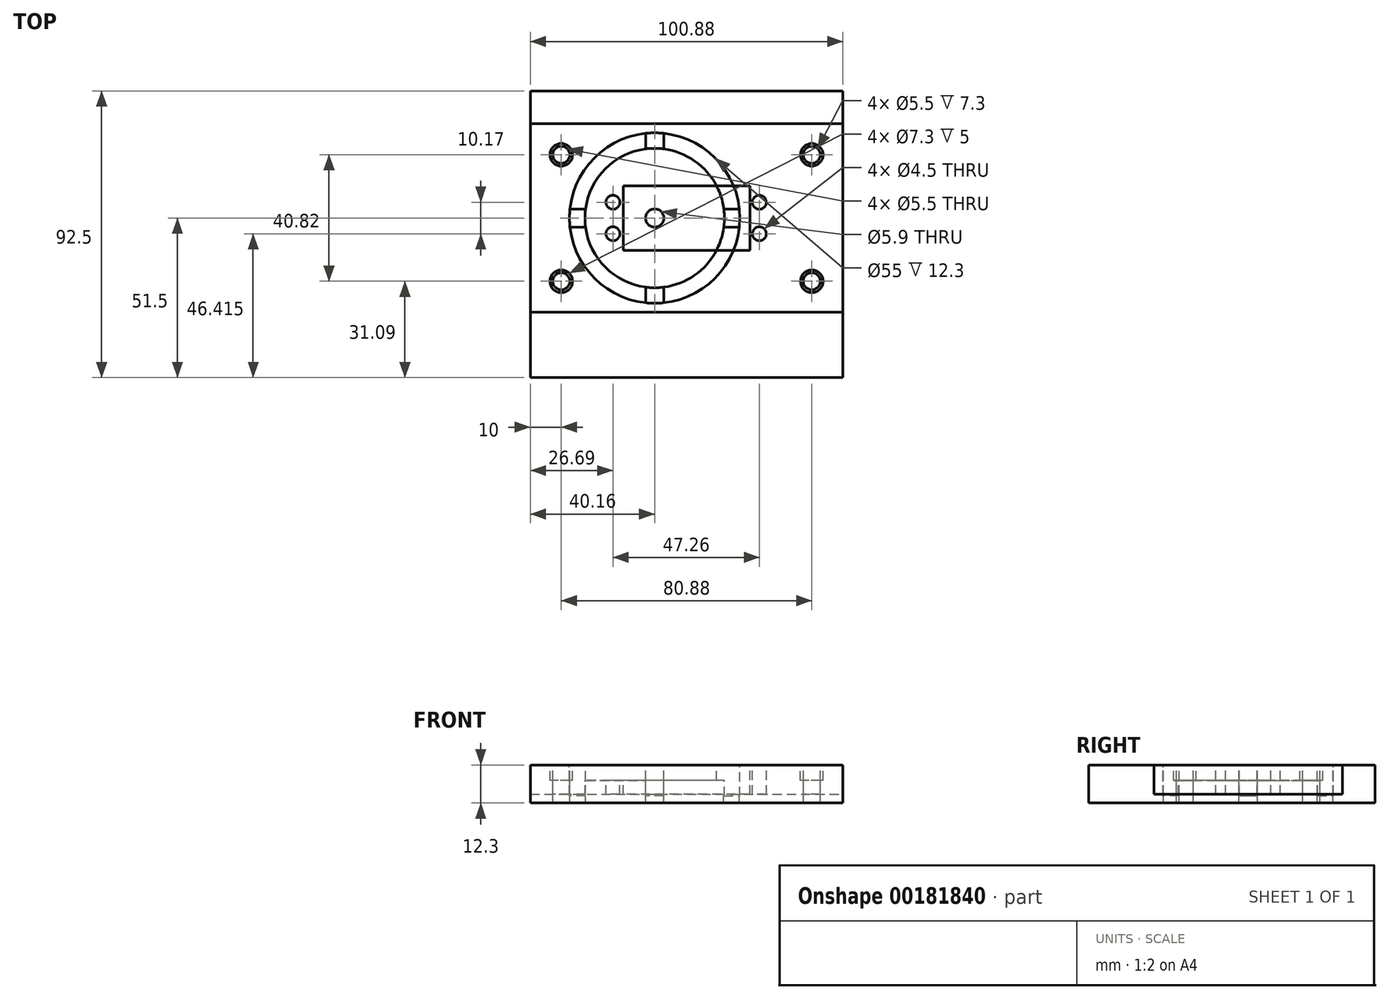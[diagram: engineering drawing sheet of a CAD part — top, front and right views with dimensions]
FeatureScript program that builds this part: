
annotation { "Feature Type Name" : "Feature", "Feature Type Description" : "" }
export const myFeature = defineFeature(function(context is Context, id is Id, definition is map)
    precondition{}
    {
        {
            var Q0;
            Q0=qCreatedBy(makeId("Top.planeOp"),FACE);
            var sketch = newSketch(context, id + "F0", { "sketchPlane" : qUnion([Q0])});
            skPoint(sketch, "E0.middle", {"position": v(0, 0) * mm});
            skLineSegment(sketch, "E1.bottom", {"start": v(19.94, 9.9) * mm, "end": v(-19.94, 9.9) * mm});
            skLineSegment(sketch, "E1.top", {"start": v(19.94, -9.91) * mm, "end": v(-19.94, -9.91) * mm});
            skLineSegment(sketch, "E1.left", {"start": v(19.94, 9.9) * mm, "end": v(19.94, -9.9) * mm});
            skLineSegment(sketch, "E1.right", {"start": v(-19.94, 9.9) * mm, "end": v(-19.94, -9.9) * mm});
            skPoint(sketch, "E2", {"position": v(-23.75, 5.08) * mm});
            skPoint(sketch, "E3", {"position": v(-23.75, -5.09) * mm});
            skPoint(sketch, "E4", {"position": v(23.5, 5.08) * mm});
            skPoint(sketch, "E5", {"position": v(23.5, -5.09) * mm});
            skPoint(sketch, "E6", {"position": v(-10.28, 0) * mm});
            skCircle(sketch, "E7", {"center": v(-23.75, 5.08) * mm, "radius": 2.19 * mm});
            skCircle(sketch, "E8", {"center": v(-23.75, -5.09) * mm, "radius": 2.19 * mm});
            skCircle(sketch, "E9", {"center": v(23.5, 5.08) * mm, "radius": 2.19 * mm});
            skCircle(sketch, "E10", {"center": v(23.5, -5.09) * mm, "radius": 2.19 * mm});
            skLineSegment(sketch, "E11", {"start": v(-19.94, 9.9) * mm, "end": v(-26.42, 9.9) * mm});
            skLineSegment(sketch, "E12", {"start": v(-26.42, 9.9) * mm, "end": v(-26.42, -9.91) * mm});
            skLineSegment(sketch, "E13", {"start": v(-26.42, -9.91) * mm, "end": v(-19.94, -9.91) * mm});
            skLineSegment(sketch, "E14", {"start": v(19.94, -9.91) * mm, "end": v(26.42, -9.91) * mm});
            skLineSegment(sketch, "E15", {"start": v(26.42, -9.9) * mm, "end": v(26.42, 9.91) * mm});
            skLineSegment(sketch, "E16", {"start": v(26.42, 9.9) * mm, "end": v(19.94, 9.9) * mm});
            skSolve(sketch);
        }
        {
            var Q0;
            Q0=qCreatedBy(makeId("Top.planeOp"),FACE);
            var sketch = newSketch(context, id + "F1", { "sketchPlane" : qUnion([Q0])});
            skPoint(sketch, "E17.0", {"position": v(-19.94, 9.9) * mm});
            skPoint(sketch, "E18.0", {"position": v(-19.94, -9.9) * mm});
            skPoint(sketch, "E19.0", {"position": v(19.94, -9.9) * mm});
            skPoint(sketch, "E20.0", {"position": v(19.94, 9.9) * mm});
            skPoint(sketch, "E21.0", {"position": v(-23.75, 5.08) * mm});
            skPoint(sketch, "E22.0", {"position": v(-23.75, -5.09) * mm});
            skPoint(sketch, "E23.0", {"position": v(23.5, -5.09) * mm});
            skPoint(sketch, "E24.0", {"position": v(23.5, 5.08) * mm});
            skLineSegment(sketch, "E25", {"start": v(-19.94, 9.9) * mm, "end": v(-19.94, -9.9) * mm, "construction": true});
            skLineSegment(sketch, "E26", {"start": v(19.94, -9.9) * mm, "end": v(19.94, 9.9) * mm, "construction": true});
            skLineSegment(sketch, "E27", {"start": v(-19.94, 9.9) * mm, "end": v(19.94, 9.9) * mm, "construction": true});
            skLineSegment(sketch, "E28", {"start": v(19.94, -9.9) * mm, "end": v(-19.94, -9.9) * mm, "construction": true});
            skLineSegment(sketch, "E29.0", {"start": v(20.44, -10.41) * mm, "end": v(20.44, 10.4) * mm});
            skLineSegment(sketch, "E29.1", {"start": v(-20.44, -10.41) * mm, "end": v(20.44, -10.41) * mm});
            skLineSegment(sketch, "E29.2", {"start": v(-20.44, 10.4) * mm, "end": v(-20.44, -10.41) * mm});
            skLineSegment(sketch, "E29.3", {"start": v(20.44, 10.4) * mm, "end": v(-20.44, 10.4) * mm});
            skPoint(sketch, "E30", {"position": v(-40.44, 20.41) * mm});
            skPoint(sketch, "E31", {"position": v(-40.44, -20.41) * mm});
            skPoint(sketch, "E32", {"position": v(40.44, 20.41) * mm});
            skPoint(sketch, "E33", {"position": v(40.44, -20.4) * mm});
            skLineSegment(sketch, "E34", {"start": v(50.44, 30.41) * mm, "end": v(-50.44, 30.4) * mm});
            skLineSegment(sketch, "E35", {"start": v(-50.44, 30.4) * mm, "end": v(-50.44, -30.41) * mm});
            skLineSegment(sketch, "E36", {"start": v(-50.44, -30.41) * mm, "end": v(50.44, -30.41) * mm});
            skLineSegment(sketch, "E37", {"start": v(50.44, -30.41) * mm, "end": v(50.44, 30.41) * mm});
            skSolve(sketch);
        }
        {
            var Q0;
            Q0=makeQuery(id+"F1.imprint","IMPRINT",FACE,{"disambiguationData":[TD([[makeQuery(id+"F1.imprint","IMPRINT",EDGE,{"derivedFrom":sQuery(id+"F1.wireOp",EDGE,"E29.0")}),-1.0]])]});
            extrude(context, id + "F2", {"entities" : qUnion([Q0]), "oppositeDirection" : true, "depth" : 9.5 * mm});
        }
        {
            var Q0;
            Q0=sQuery(id+"F0.wireOp",VERTEX,"E2");
            var Q1;
            Q1=sQuery(id+"F0.wireOp",VERTEX,"E3");
            var Q2;
            Q2=sQuery(id+"F0.wireOp",VERTEX,"E5");
            var Q3;
            Q3=sQuery(id+"F0.wireOp",VERTEX,"E4");
            var Q4;
            Q4=sQuery(id+"F0.wireOp",VERTEX,"E5");
            var Q5;
            Q5=makeQuery(id+"F2.opExtrude","SWEPT_BODY",BODY,{"disambiguationData":[OSD([sQuery(id+"F1.wireOp",EDGE,"E29.0"),sQuery(id+"F1.wireOp",EDGE,"E29.1"),sQuery(id+"F1.wireOp",EDGE,"E29.2"),sQuery(id+"F1.wireOp",EDGE,"E29.3"),sQuery(id+"F1.wireOp",EDGE,"ceac850b-cf01-4485-95b4-8c1f3a94b1ee.0"),sQuery(id+"F1.wireOp",EDGE,"ceac850b-cf01-4485-95b4-8c1f3a94b1ee.1"),sQuery(id+"F1.wireOp",EDGE,"ceac850b-cf01-4485-95b4-8c1f3a94b1ee.2"),sQuery(id+"F1.wireOp",EDGE,"ceac850b-cf01-4485-95b4-8c1f3a94b1ee.3")])]});
            hole(context, id + "F3", {"style" : HoleStyle.SIMPLE, "endStyle" : HoleEndStyle.THROUGH, "holeDiameter" : 4.5 * mm, "startFromSketch" : true, "locations" : qUnion([Q0, Q1, Q2, Q3, Q4]), "scope" : qUnion([Q5]), "isTappedThrough" : true});
        }
        {
            var Q0;
            Q0=sQuery(id+"F1.wireOp",VERTEX,"E30");
            var Q1;
            Q1=sQuery(id+"F1.wireOp",VERTEX,"E31");
            var Q2;
            Q2=sQuery(id+"F1.wireOp",VERTEX,"E33");
            var Q3;
            Q3=sQuery(id+"F1.wireOp",VERTEX,"E32");
            var Q4;
            Q4=makeQuery(id+"F2.opExtrude","SWEPT_BODY",BODY,{"disambiguationData":[OSD([sQuery(id+"F1.wireOp",EDGE,"E29.0"),sQuery(id+"F1.wireOp",EDGE,"E29.1"),sQuery(id+"F1.wireOp",EDGE,"E29.2"),sQuery(id+"F1.wireOp",EDGE,"E29.3"),sQuery(id+"F1.wireOp",EDGE,"ceac850b-cf01-4485-95b4-8c1f3a94b1ee.0"),sQuery(id+"F1.wireOp",EDGE,"ceac850b-cf01-4485-95b4-8c1f3a94b1ee.1"),sQuery(id+"F1.wireOp",EDGE,"ceac850b-cf01-4485-95b4-8c1f3a94b1ee.2"),sQuery(id+"F1.wireOp",EDGE,"ceac850b-cf01-4485-95b4-8c1f3a94b1ee.3")])]});
            hole(context, id + "F4", {"style" : HoleStyle.SIMPLE, "endStyle" : HoleEndStyle.THROUGH, "holeDiameter" : 5.5 * mm, "startFromSketch" : true, "locations" : qUnion([Q0, Q1, Q2, Q3]), "scope" : qUnion([Q4]), "isTappedThrough" : true});
        }
        {
            var Q0;
            Q0=qCreatedBy(makeId("Top.planeOp"),FACE);
            var sketch = newSketch(context, id + "F5", { "sketchPlane" : qUnion([Q0])});
            skLineSegment(sketch, "E38.bottom", {"start": v(-50.44, 41) * mm, "end": v(50.44, 41) * mm});
            skLineSegment(sketch, "E38.top", {"start": v(-50.44, -51.5) * mm, "end": v(50.44, -51.5) * mm});
            skLineSegment(sketch, "E38.left", {"start": v(-50.44, 41) * mm, "end": v(-50.44, -51.5) * mm});
            skLineSegment(sketch, "E38.right", {"start": v(50.44, 41) * mm, "end": v(50.44, -51.5) * mm});
            skLineSegment(sketch, "E39", {"start": v(-50.44, 0) * mm, "end": v(-10.28, 0) * mm, "construction": true});
            skCircle(sketch, "E40", {"center": v(-10.28, 0) * mm, "radius": 2.95 * mm});
            skCircle(sketch, "E41", {"center": v(-10.28, 0) * mm, "radius": 22.5 * mm});
            skCircle(sketch, "E42", {"center": v(-10.28, 0) * mm, "radius": 27.5 * mm});
            skLineSegment(sketch, "E43", {"start": v(-7.33, 22.3) * mm, "end": v(-7.33, -22.3) * mm, "construction": true});
            skLineSegment(sketch, "E44", {"start": v(-13.23, 22.3) * mm, "end": v(-13.23, -22.3) * mm, "construction": true});
            skLineSegment(sketch, "E45", {"start": v(-32.59, 2.95) * mm, "end": v(12.03, 2.95) * mm, "construction": true});
            skLineSegment(sketch, "E46", {"start": v(-32.59, -2.95) * mm, "end": v(12.03, -2.95) * mm, "construction": true});
            skLineSegment(sketch, "E47", {"start": v(-13.23, 22.3) * mm, "end": v(-13.23, 27.34) * mm});
            skLineSegment(sketch, "E48", {"start": v(-7.33, 22.3) * mm, "end": v(-7.33, 27.34) * mm});
            skLineSegment(sketch, "E49", {"start": v(12.03, 2.95) * mm, "end": v(17.06, 2.95) * mm});
            skLineSegment(sketch, "E50", {"start": v(12.03, -2.95) * mm, "end": v(17.06, -2.95) * mm});
            skLineSegment(sketch, "E51", {"start": v(-7.33, -22.3) * mm, "end": v(-7.33, -27.34) * mm});
            skLineSegment(sketch, "E52", {"start": v(-13.23, -22.3) * mm, "end": v(-13.23, -27.34) * mm});
            skLineSegment(sketch, "E53", {"start": v(-32.59, -2.95) * mm, "end": v(-37.62, -2.95) * mm});
            skLineSegment(sketch, "E54", {"start": v(-32.59, 2.95) * mm, "end": v(-37.62, 2.95) * mm});
            skPoint(sketch, "E55.0", {"position": v(-40.44, 20.41) * mm});
            skPoint(sketch, "E56.0", {"position": v(-40.44, -20.41) * mm});
            skPoint(sketch, "E57.0", {"position": v(40.44, -20.4) * mm});
            skPoint(sketch, "E58.0", {"position": v(40.44, 20.41) * mm});
            skSolve(sketch);
        }
        {
            var Q0;
            Q0=makeQuery(id+"F5.imprint","IMPRINT",FACE,{"disambiguationData":[TD([[makeQuery(id+"F5.imprint","IMPRINT",EDGE,{"derivedFrom":sQuery(id+"F5.wireOp",EDGE,"E38.bottom")}),-1.0]])]});
            var Q1;
            {var subQ0=sQuery(id+"F5.wireOp",EDGE,"E53");Q1=makeQuery(id+"F5.imprint","IMPRINT",FACE,{"disambiguationData":[TD([[makeQuery(id+"F5.imprint","IMPRINT",EDGE,{"derivedFrom":subQ0}),-1.0]])]});}
            var Q2;
            Q2=makeQuery(id+"F5.imprint","IMPRINT",FACE,{"disambiguationData":[TD([[makeQuery(id+"F5.imprint","IMPRINT",EDGE,{"derivedFrom":sQuery(id+"F5.wireOp",EDGE,"E40")}),-1.0]])]});
            var Q3;
            {var subQ0=sQuery(id+"F5.wireOp",EDGE,"E47");Q3=makeQuery(id+"F5.imprint","IMPRINT",FACE,{"disambiguationData":[TD([[makeQuery(id+"F5.imprint","IMPRINT",EDGE,{"derivedFrom":subQ0}),-1.0]])]});}
            var Q4;
            {var subQ0=sQuery(id+"F5.wireOp",EDGE,"E49");Q4=makeQuery(id+"F5.imprint","IMPRINT",FACE,{"disambiguationData":[TD([[makeQuery(id+"F5.imprint","IMPRINT",EDGE,{"derivedFrom":subQ0}),-1.0]])]});}
            var Q5;
            {var subQ0=sQuery(id+"F5.wireOp",EDGE,"E51");Q5=makeQuery(id+"F5.imprint","IMPRINT",FACE,{"disambiguationData":[TD([[makeQuery(id+"F5.imprint","IMPRINT",EDGE,{"derivedFrom":subQ0}),-1.0]])]});}
            extrude(context, id + "F6", {"entities" : qUnion([Q0, Q1, Q2, Q3, Q4, Q5]), "oppositeDirection" : true, "depth" : 12.3 * mm});
        }
        {
            var Q0;
            {var subQ0=sQuery(id+"F5.wireOp",EDGE,"E47");Q0=makeQuery(id+"F5.imprint","IMPRINT",FACE,{"disambiguationData":[TD([[makeQuery(id+"F5.imprint","IMPRINT",EDGE,{"derivedFrom":subQ0}),-1.0]])]});}
            var Q1;
            {var subQ0=sQuery(id+"F5.wireOp",EDGE,"E53");Q1=makeQuery(id+"F5.imprint","IMPRINT",FACE,{"disambiguationData":[TD([[makeQuery(id+"F5.imprint","IMPRINT",EDGE,{"derivedFrom":subQ0}),-1.0]])]});}
            var Q2;
            {var subQ0=sQuery(id+"F5.wireOp",EDGE,"E51");Q2=makeQuery(id+"F5.imprint","IMPRINT",FACE,{"disambiguationData":[TD([[makeQuery(id+"F5.imprint","IMPRINT",EDGE,{"derivedFrom":subQ0}),-1.0]])]});}
            var Q3;
            {var subQ0=sQuery(id+"F5.wireOp",EDGE,"E49");Q3=makeQuery(id+"F5.imprint","IMPRINT",FACE,{"disambiguationData":[TD([[makeQuery(id+"F5.imprint","IMPRINT",EDGE,{"derivedFrom":subQ0}),-1.0]])]});}
            extrude(context, id + "F7", {"entities" : qUnion([Q0, Q1, Q2, Q3]), "operationType" : NewBodyOperationType.REMOVE, "oppositeDirection" : true, "depth" : 10 * mm});
        }
        {
            var Q0;
            Q0=makeQuery(id+"F5.imprint","IMPRINT",FACE,{"disambiguationData":[TD([[makeQuery(id+"F5.imprint","IMPRINT",EDGE,{"derivedFrom":sQuery(id+"F5.wireOp",EDGE,"E40")}),-1.0]])]});
            extrude(context, id + "F8", {"entities" : qUnion([Q0]), "operationType" : NewBodyOperationType.REMOVE, "oppositeDirection" : true, "depth" : 5 * mm});
        }
        {
            var Q0;
            Q0=sQuery(id+"F1.wireOp",VERTEX,"E30");
            var Q1;
            Q1=sQuery(id+"F1.wireOp",VERTEX,"E31");
            var Q2;
            Q2=sQuery(id+"F1.wireOp",VERTEX,"E33");
            var Q3;
            Q3=sQuery(id+"F1.wireOp",VERTEX,"E32");
            var Q4;
            Q4=makeQuery(id+"F6.opExtrude","SWEPT_BODY",BODY,{"disambiguationData":[OSD([sQuery(id+"F5.wireOp",EDGE,"E38.bottom"),sQuery(id+"F5.wireOp",EDGE,"E38.top"),sQuery(id+"F5.wireOp",EDGE,"E38.left"),sQuery(id+"F5.wireOp",EDGE,"E38.right"),sQuery(id+"F5.wireOp",EDGE,"E40"),sQuery(id+"F5.wireOp",EDGE,"E41"),sQuery(id+"F5.wireOp",EDGE,"E42"),sQuery(id+"F5.wireOp",EDGE,"E47"),sQuery(id+"F5.wireOp",EDGE,"E48"),sQuery(id+"F5.wireOp",EDGE,"E49"),sQuery(id+"F5.wireOp",EDGE,"E50"),sQuery(id+"F5.wireOp",EDGE,"E51"),sQuery(id+"F5.wireOp",EDGE,"E52"),sQuery(id+"F5.wireOp",EDGE,"E53"),sQuery(id+"F5.wireOp",EDGE,"E54")])]});
            hole(context, id + "F9", {"style" : HoleStyle.C_BORE, "endStyle" : HoleEndStyle.THROUGH, "holeDiameter" : 5.5 * mm, "cBoreDiameter" : 7.3 * mm, "cBoreDepth" : 5 * mm, "startFromSketch" : true, "locations" : qUnion([Q0, Q1, Q2, Q3]), "scope" : qUnion([Q4]), "isTappedThrough" : true});
        }
    });
